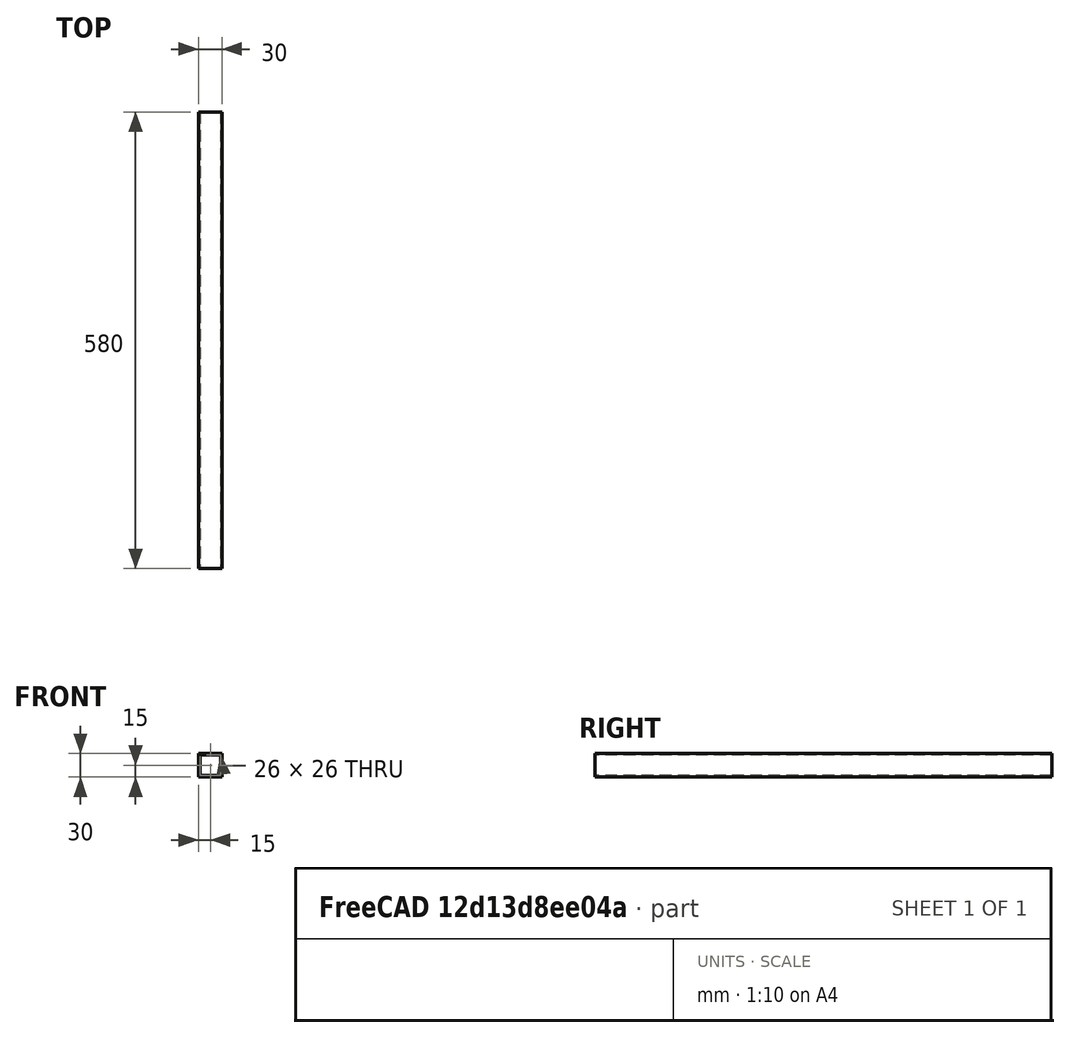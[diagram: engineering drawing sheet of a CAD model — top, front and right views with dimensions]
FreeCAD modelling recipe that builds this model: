
FCSTD DOCUMENT  (FreeCAD 0.20R29603 (Git))
Label: AluProfil 30x30x2_längs
License: All rights reserved
LicenseURL: http://en.wikipedia.org/wiki/All_rights_reserved
objects: Sketcher::SketchObject×1, PartDesign::Pad×1, PartDesign::Body×1
note: 4 computed .brp shape members not serialized (recipe doc carries the construction recipe); baked Part::Feature solids carry a one-line shape summary decoded from their .brp

FEATURE [Sketcher::SketchObject] Sketch002
  FullyConstrained = true
  MapMode = 5
  Placement = pos=(0,0,0) rot=(1,0,0;1.5708rad)
  Support = -> [XZ_Plane002]
  sketch-geometry (8):
    g0: LineSegment StartX=0 StartY=0 StartZ=0 EndX=30 EndY=0 EndZ=0
    g1: LineSegment StartX=30 StartY=0 StartZ=0 EndX=30 EndY=-30 EndZ=0
    g2: LineSegment StartX=30 StartY=-30 StartZ=0 EndX=0 EndY=-30 EndZ=0
    g3: LineSegment StartX=0 StartY=-30 StartZ=0 EndX=0 EndY=0 EndZ=0
    g4: LineSegment StartX=2 StartY=-2 StartZ=0 EndX=28 EndY=-2 EndZ=0
    g5: LineSegment StartX=28 StartY=-2 StartZ=0 EndX=28 EndY=-28 EndZ=0
    g6: LineSegment StartX=28 StartY=-28 StartZ=0 EndX=2 EndY=-28 EndZ=0
    g7: LineSegment StartX=2 StartY=-28 StartZ=0 EndX=2 EndY=-2 EndZ=0
  constraints (24):
    c: Coincident(g0,g1)
    c: Coincident(g1,g2)
    c: Coincident(g2,g3)
    c: Coincident(g3,g0)
    c: Horizontal(g0)
    c: Horizontal(g2)
    c: Vertical(g1)
    c: Vertical(g3)
    c: PointOnObject(g0,g-2)
    c: Coincident(g4,g5)
    c: Coincident(g5,g6)
    c: Coincident(g6,g7)
    c: Coincident(g7,g4)
    c: Horizontal(g4)
    c: Horizontal(g6)
    c: Vertical(g5)
    c: Vertical(g7)
    c: Distance(g0) = 30
    c: Distance(g1) = 30
    c: Distance(g4) = 26
    c: Distance(g5) = 26
    c: Distance(g2,g7) = 2
    c: Distance(g4,g0) = 2
    c: PointOnObject(g0,g-1)
FEATURE [PartDesign::Pad] Pad002  label="länge 840mm001"
  Direction = (0,-1,-2e-16)
  Length = 580
  Length2 = 10
  Placement = pos=(0,0,0) rot=(1,0,0;1.5708rad)
  Profile = -> Sketch002
  ReferenceAxis = -> Sketch002 [N_Axis]
  Type = 0
FEATURE [PartDesign::Body] Body002  label="AluProfil 30x30x2 003"
  Group = -> [Sketch002,Pad002]
  Origin = -> Origin002
  Tip = -> Pad002
